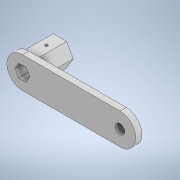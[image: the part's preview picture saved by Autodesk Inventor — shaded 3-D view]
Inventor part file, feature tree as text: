
AUTODESK INVENTOR PART (.ipt)
format: ipt  version: 2022 (Build 260153000, 153)  size: 164,352 bytes
history: native  units: mm
features: sketch x4, extrude x4, projected_geometry x2, plane x1
ambient origin geometry x8: Origin, YZ Plane, XZ Plane, XY Plane, X Axis, Y Axis, Z Axis, Center Point
bodies: Solid1 (feature_tree)
feature tree (11):
  plane  "Work Plane4"
  sketch  "Sketch3"  dims[d5=4.6mm d13=15.0mm]
  extrude  "Extrusion5"  Depth=15.0mm
  extrude  "Extrusion6"  Depth=3.0mm TaperAngle=0.0deg
  extrude  "Extrusion7"  Depth=60.0mm TaperAngle=360.0deg
  extrude  "Extrusion8"  Depth=2.5mm
  sketch  "Sketch6"  dims[d14=47.0mm d15=3.0mm d16=0.0mm]
  sketch  "Sketch7"  dims[d17=3.1mm d18=60.0mm d20=360.0deg]
  projected_geometry  "Projected Loop2"
  sketch  "Sketch8"  dims[d22=0.4mm d23=2.5mm d24=15.0mm d25=0.0mm d26=15.0mm d27=0.0mm d29=1.3mm d30=11.5mm d31=15.0mm d32=0.0mm]
  projected_geometry  "Projected Loop3"
